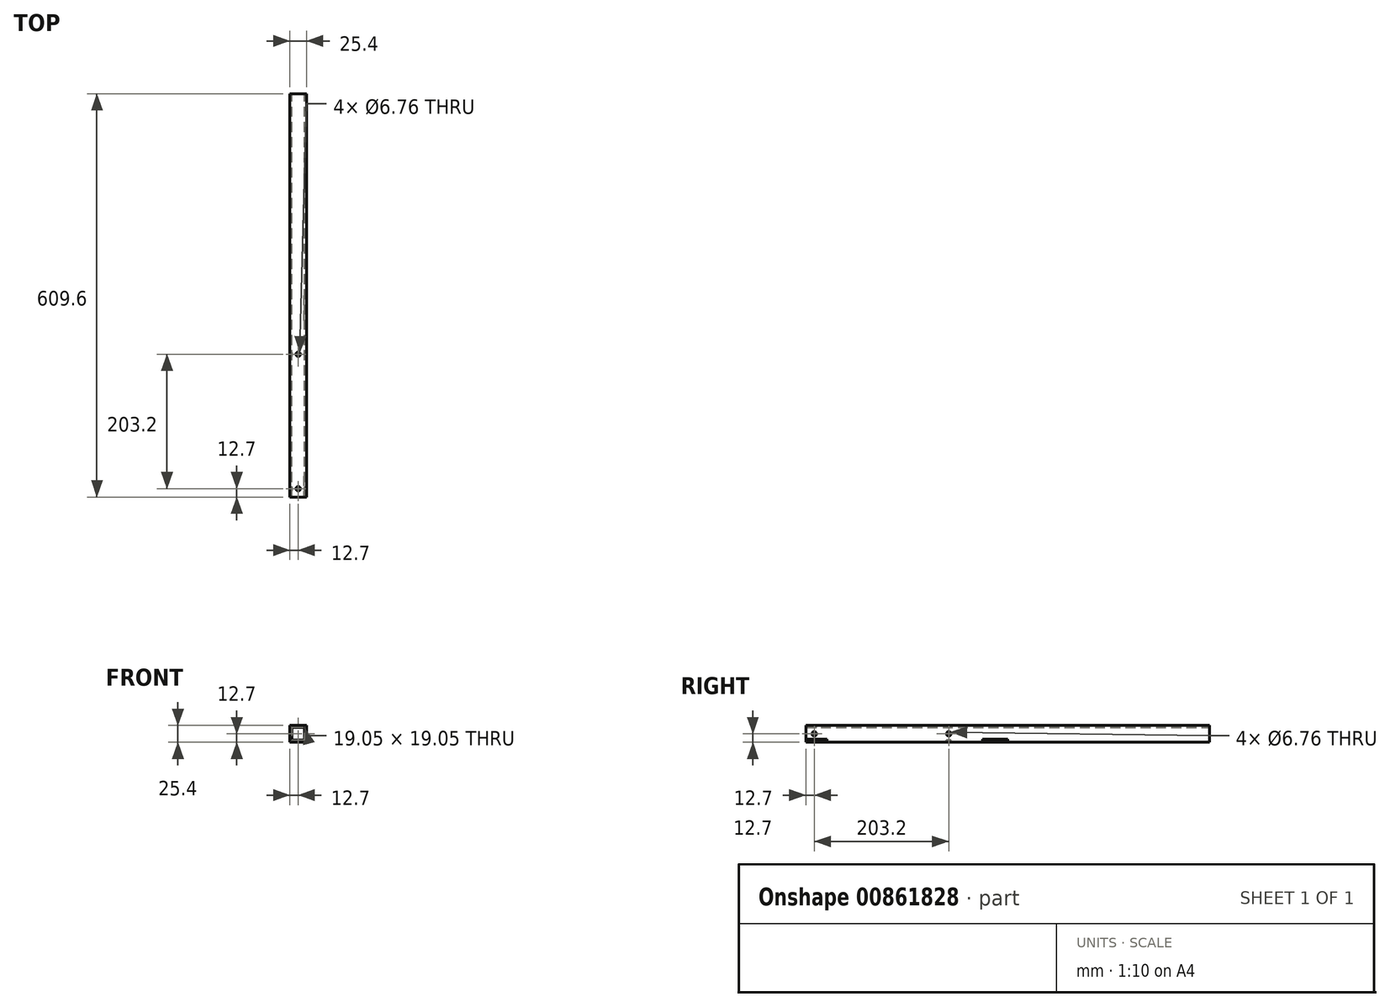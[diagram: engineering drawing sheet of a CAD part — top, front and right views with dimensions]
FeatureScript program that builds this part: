
annotation { "Feature Type Name" : "Feature", "Feature Type Description" : "" }
export const myFeature = defineFeature(function(context is Context, id is Id, definition is map)
    precondition{}
    {
        {
            var Q0;
            Q0=qCreatedBy(makeId("Front.planeOp"),FACE);
            var sketch = newSketch(context, id + "F0", { "sketchPlane" : qUnion([Q0])});
            skLineSegment(sketch, "E0.bottom", {"start": v(12.7, 12.7) * mm, "end": v(-12.7, 12.7) * mm});
            skLineSegment(sketch, "E0.top", {"start": v(12.7, -12.7) * mm, "end": v(-12.7, -12.7) * mm});
            skLineSegment(sketch, "E0.left", {"start": v(12.7, 12.7) * mm, "end": v(12.7, -12.7) * mm});
            skLineSegment(sketch, "E0.right", {"start": v(-12.7, 12.7) * mm, "end": v(-12.7, -12.7) * mm});
            skPoint(sketch, "E0.middle", {"position": v(0, 0) * mm});
            skLineSegment(sketch, "E1.bottom", {"start": v(9.53, 9.53) * mm, "end": v(-9.53, 9.53) * mm});
            skLineSegment(sketch, "E1.top", {"start": v(9.53, -9.53) * mm, "end": v(-9.53, -9.53) * mm});
            skLineSegment(sketch, "E1.left", {"start": v(9.53, 9.53) * mm, "end": v(9.53, -9.53) * mm});
            skLineSegment(sketch, "E1.right", {"start": v(-9.53, 9.53) * mm, "end": v(-9.53, -9.53) * mm});
            skSolve(sketch);
        }
        {
            var Q0;
            Q0 = qSketchRegion(id + "F0", true);
            extrude(context, id + "F1", {"entities" : qUnion([Q0]), "depth" : 609.6 * mm, "offsetDistance" : 25.4 * mm, "symmetric" : true});
        }
        {
            var Q0;
            Q0=makeQuery(id+"F1.opExtrude","SWEPT_FACE",FACE,{"disambiguationData":[OSD([sQuery(id+"F0.wireOp",EDGE,"E0.bottom")])]});
            var sketch = newSketch(context, id + "F2", { "sketchPlane" : qUnion([Q0])});
            skCircle(sketch, "E2", {"center": v(0, -292.1) * mm, "radius": 3.38 * mm});
            skCircle(sketch, "E3", {"center": v(0, -88.9) * mm, "radius": 3.38 * mm});
            skSolve(sketch);
        }
        {
            var Q0;
            Q0 = qSketchRegion(id + "F2", true);
            var Q1;
            Q1=makeQuery(id+"F1.opExtrude","SWEPT_FACE",FACE,{"disambiguationData":[OSD([sQuery(id+"F0.wireOp",EDGE,"E0.top")])]});
            extrude(context, id + "F3", {"entities" : qUnion([Q0]), "operationType" : NewBodyOperationType.REMOVE, "endBound" : BoundingType.UP_TO_SURFACE, "oppositeDirection" : true, "depth" : 25.4 * mm, "endBoundEntityFace" : qUnion([Q1]), "offsetDistance" : 25.4 * mm});
        }
        {
            var Q0;
            Q0=makeQuery(id+"F1.opExtrude","SWEPT_FACE",FACE,{"disambiguationData":[OSD([sQuery(id+"F0.wireOp",EDGE,"E0.left")])]});
            var sketch = newSketch(context, id + "F4", { "sketchPlane" : qUnion([Q0])});
            skCircle(sketch, "E4", {"center": v(-292.1, 0) * mm, "radius": 3.38 * mm});
            skCircle(sketch, "E5", {"center": v(-88.9, 0) * mm, "radius": 3.38 * mm});
            skSolve(sketch);
        }
        {
            var Q0;
            Q0 = qSketchRegion(id + "F4", true);
            var Q1;
            Q1=makeQuery(id+"F1.opExtrude","SWEPT_FACE",FACE,{"disambiguationData":[OSD([sQuery(id+"F0.wireOp",EDGE,"E0.right")])]});
            extrude(context, id + "F5", {"entities" : qUnion([Q0]), "operationType" : NewBodyOperationType.REMOVE, "endBound" : BoundingType.UP_TO_SURFACE, "oppositeDirection" : true, "depth" : 25.4 * mm, "endBoundEntityFace" : qUnion([Q1]), "offsetDistance" : 25.4 * mm});
        }
        {
            var Q0;
            Q0=makeQuery(id+"F1.opExtrude","CAP_FACE",FACE,{"disambiguationData":[OSD([sQuery(id+"F0.wireOp",EDGE,"E0.bottom"),sQuery(id+"F0.wireOp",EDGE,"E0.top"),sQuery(id+"F0.wireOp",EDGE,"E0.left"),sQuery(id+"F0.wireOp",EDGE,"E0.right"),sQuery(id+"F0.wireOp",EDGE,"E1.bottom"),sQuery(id+"F0.wireOp",EDGE,"E1.top"),sQuery(id+"F0.wireOp",EDGE,"E1.left"),sQuery(id+"F0.wireOp",EDGE,"E1.right")])],"isStart":false});
            var sketch = newSketch(context, id + "F6", { "sketchPlane" : qUnion([Q0])});
            skLineSegment(sketch, "E6", {"start": v(12.7, -7.94) * mm, "end": v(7.94, -12.7) * mm});
            skLineSegment(sketch, "E7", {"start": v(7.94, -12.7) * mm, "end": v(12.7, -12.7) * mm});
            skLineSegment(sketch, "E8", {"start": v(12.7, -12.7) * mm, "end": v(12.7, -7.94) * mm});
            skSolve(sketch);
        }
        {
            var Q0;
            Q0 = qSketchRegion(id + "F6", true);
            extrude(context, id + "F7", {"entities" : qUnion([Q0]), "operationType" : NewBodyOperationType.REMOVE, "oppositeDirection" : true, "depth" : 31.75 * mm, "offsetDistance" : 25.4 * mm});
        }
        {
            var Q0;
            Q0=makeQuery(id+"F1.opExtrude","CAP_FACE",FACE,{"disambiguationData":[OSD([sQuery(id+"F0.wireOp",EDGE,"E0.bottom"),sQuery(id+"F0.wireOp",EDGE,"E0.top"),sQuery(id+"F0.wireOp",EDGE,"E0.left"),sQuery(id+"F0.wireOp",EDGE,"E0.right"),sQuery(id+"F0.wireOp",EDGE,"E1.bottom"),sQuery(id+"F0.wireOp",EDGE,"E1.top"),sQuery(id+"F0.wireOp",EDGE,"E1.left"),sQuery(id+"F0.wireOp",EDGE,"E1.right")])],"isStart":false});
            cPlane(context, id + "F8", {"entities" : qUnion([Q0]), "cplaneType" : CPlaneType.OFFSET, "offset" : 266.7 * mm, "oppositeDirection" : true, "width" : 152.4 * mm, "height" : 152.4 * mm});
        }
        {
            var Q0;
            Q0=qCreatedBy(id+"F8.planeOp",FACE);
            var sketch = newSketch(context, id + "F9", { "sketchPlane" : qUnion([Q0])});
            skLineSegment(sketch, "E9.0", {"start": v(12.7, -7.94) * mm, "end": v(7.94, -12.7) * mm});
            skLineSegment(sketch, "E10.0", {"start": v(12.7, -12.7) * mm, "end": v(7.94, -12.7) * mm});
            skLineSegment(sketch, "E11.0", {"start": v(12.7, -7.94) * mm, "end": v(12.7, -12.7) * mm});
            skSolve(sketch);
        }
        {
            var Q0;
            Q0 = qSketchRegion(id + "F9", true);
            extrude(context, id + "F10", {"entities" : qUnion([Q0]), "operationType" : NewBodyOperationType.REMOVE, "oppositeDirection" : true, "depth" : 38.1 * mm, "offsetDistance" : 25.4 * mm});
        }
    });
